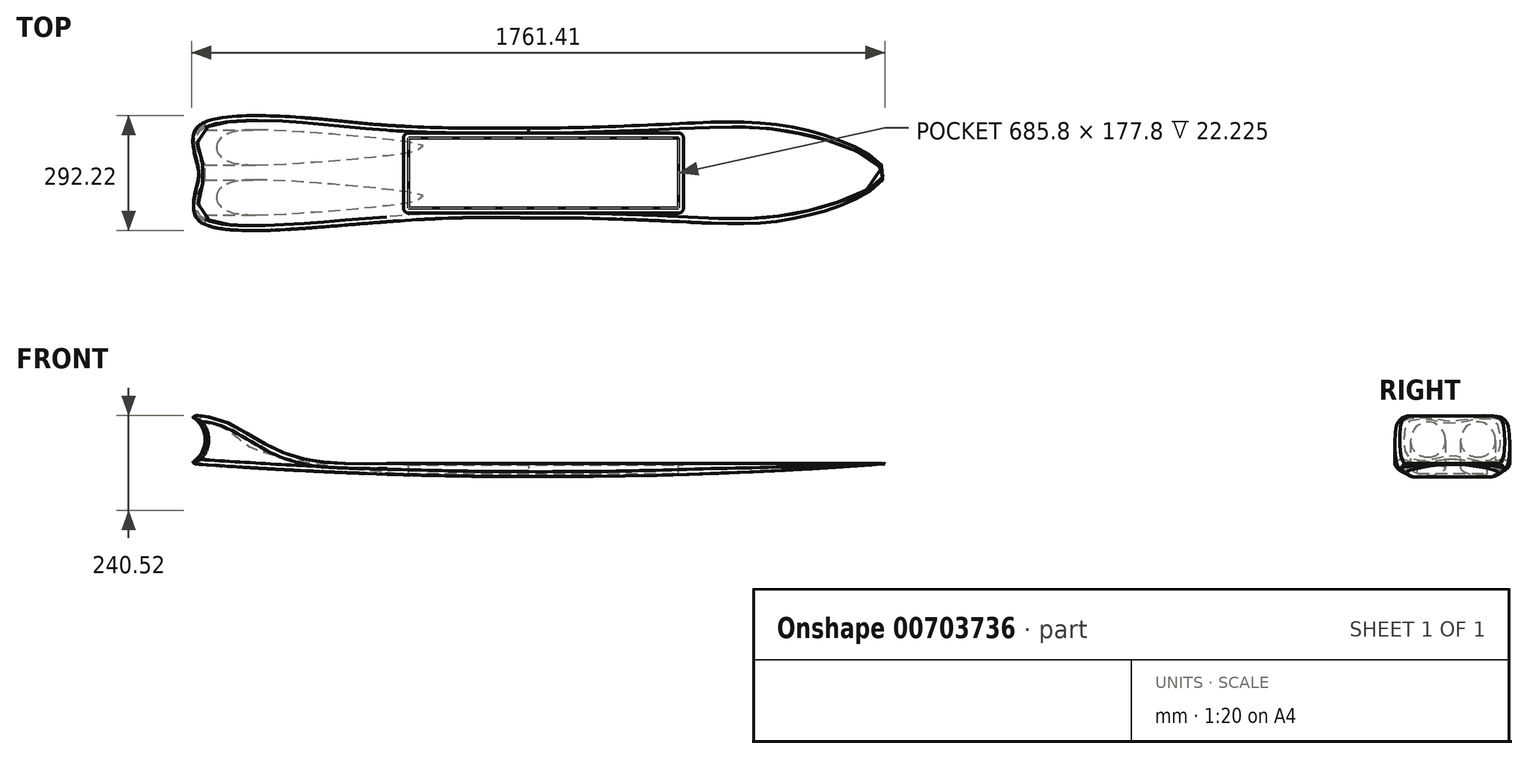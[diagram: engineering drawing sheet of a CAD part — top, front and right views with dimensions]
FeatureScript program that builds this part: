
annotation { "Feature Type Name" : "Feature", "Feature Type Description" : "" }
export const myFeature = defineFeature(function(context is Context, id is Id, definition is map)
    precondition{}
    {
        {
            var Q0;
            Q0=qCreatedBy(makeId("Front.planeOp"),FACE);
            var sketch = newSketch(context, id + "F0", { "sketchPlane" : qUnion([Q0])});
            skArc(sketch, "E0", {"start": v(-860.12, 0) * mm, "mid": v(28.88, -33.4) * mm, "end": v(917.88, 0) * mm});
            skArc(sketch, "E1", {"start": v(-860.12, 0) * mm, "mid": v(-821.37, 62.98) * mm, "end": v(-864.4, 123.1) * mm});
            skLineSegment(sketch, "E2", {"start": v(-360.96, 0) * mm, "end": v(917.88, 0) * mm});
            skFitSpline(sketch, "E3", {"points": [v(-864.4, 123.1) * mm, v(-768.9, 105.74) * mm, v(-612.6, 23.25) * mm, v(-360.96, 0) * mm], "startDerivative": vector(368.4, -19.72) * mm, "endDerivative": vector(657.62, 11.35) * mm});
            skSolve(sketch);
        }
        {
            var Q0;
            Q0=makeQuery(id+"F0.imprint","IMPRINT",FACE,{"disambiguationData":[TD([[makeQuery(id+"F0.imprint","IMPRINT",EDGE,{"derivedFrom":sQuery(id+"F0.wireOp",EDGE,"E0")}),1.0]])]});
            extrude(context, id + "F1", {"entities" : qUnion([Q0]), "endBound" : BoundingType.SYMMETRIC, "depth" : 304.8 * mm, "offsetDistance" : 25.4 * mm});
        }
        {
            var Q0;
            Q0=qCreatedBy(makeId("Top.planeOp"),FACE);
            var sketch = newSketch(context, id + "F2", { "sketchPlane" : qUnion([Q0])});
            skFitSpline(sketch, "E4", {"points": [v(0, 114.3) * mm, v(-558.8, 139.7) * mm, v(-838.2, 120.65) * mm, v(-852.96, 59.7) * mm, v(-838.2, 0) * mm, v(-850.9, -59.7) * mm, v(-838.2, -120.65) * mm, v(-558.8, -139.7) * mm, v(0, -114.3) * mm], "startDerivative": vector(-4957.76, -51.43) * mm, "endDerivative": vector(3133.64, -106.94) * mm});
            skFitSpline(sketch, "E5", {"points": [v(0, 114.3) * mm, v(685.8, 114.3) * mm, v(914.4, 0) * mm, v(685.8, -114.3) * mm, v(0, -114.3) * mm], "startDerivative": vector(3821.37, 9.43) * mm, "endDerivative": vector(-3821.37, -30.54) * mm});
            skLineSegment(sketch, "E6.bottom", {"start": v(-1371.02, 605.3) * mm, "end": v(1425.25, 605.3) * mm});
            skLineSegment(sketch, "E6.top", {"start": v(-1371.02, -634.77) * mm, "end": v(1425.25, -634.77) * mm});
            skLineSegment(sketch, "E6.left", {"start": v(-1371.02, 605.3) * mm, "end": v(-1371.02, -634.77) * mm});
            skLineSegment(sketch, "E6.right", {"start": v(1425.25, 605.3) * mm, "end": v(1425.25, -634.77) * mm});
            skSolve(sketch);
        }
        {
            var Q0;
            Q0=makeQuery(id+"F2.imprint","IMPRINT",FACE,{"disambiguationData":[TD([[makeQuery(id+"F2.imprint","IMPRINT",EDGE,{"derivedFrom":sQuery(id+"F2.wireOp",EDGE,"E4")}),-1.0]])]});
            extrude(context, id + "F3", {"entities" : qUnion([Q0]), "operationType" : NewBodyOperationType.REMOVE, "endBound" : BoundingType.SYMMETRIC, "depth" : 304.8 * mm, "offsetDistance" : 25.4 * mm});
        }
        {
            var Q0;
            Q0=makeQuery(id+"F3.boolean.opBoolean","INTERSECT",EDGE,{"derivedFrom":[makeQuery(id+"F1.opExtrude","SWEPT_FACE",FACE,{"disambiguationData":[OSD([sQuery(id+"F0.wireOp",EDGE,"E0")])]}),makeQuery(id+"F3.opExtrude","SWEPT_FACE",FACE,{"disambiguationData":[OSD([sQuery(id+"F2.wireOp",EDGE,"E4")])]})]});
            var Q1;
            Q1=makeQuery(id+"F3.boolean.opBoolean","INTERSECT",EDGE,{"derivedFrom":[makeQuery(id+"F1.opExtrude","SWEPT_FACE",FACE,{"disambiguationData":[OSD([sQuery(id+"F0.wireOp",EDGE,"E3")])]}),makeQuery(id+"F3.opExtrude","SWEPT_FACE",FACE,{"disambiguationData":[OSD([sQuery(id+"F2.wireOp",EDGE,"E4")])]})]});
            var Q2;
            Q2=makeQuery(id+"F1.opExtrude","SWEPT_FACE",FACE,{"disambiguationData":[OSD([sQuery(id+"F0.wireOp",EDGE,"E0")])]});
            var Q3;
            Q3=makeQuery(id+"F3.boolean.opBoolean","COPY",FACE,{"derivedFrom":makeQuery(id+"F3.opExtrude","SWEPT_FACE",FACE,{"disambiguationData":[OSD([sQuery(id+"F2.wireOp",EDGE,"E5")])]})});
            var Q4;
            Q4=makeQuery(id+"F3.boolean.opBoolean","COPY",FACE,{"derivedFrom":makeQuery(id+"F3.opExtrude","SWEPT_FACE",FACE,{"disambiguationData":[OSD([sQuery(id+"F2.wireOp",EDGE,"E4")])]})});
            var Q5;
            Q5=makeQuery(id+"F1.opExtrude","SWEPT_FACE",FACE,{"disambiguationData":[OSD([sQuery(id+"F0.wireOp",EDGE,"E2")])]});
            var Q6;
            Q6=makeQuery(id+"F3.boolean.opBoolean","INTERSECT",EDGE,{"derivedFrom":[makeQuery(id+"F1.opExtrude","SWEPT_FACE",FACE,{"disambiguationData":[OSD([sQuery(id+"F0.wireOp",EDGE,"E2")])]}),makeQuery(id+"F3.opExtrude","SWEPT_FACE",FACE,{"disambiguationData":[OSD([sQuery(id+"F2.wireOp",EDGE,"E5")])]})]});
            var Q7;
            Q7=makeQuery(id+"F3.boolean.opBoolean","INTERSECT",EDGE,{"derivedFrom":[makeQuery(id+"F1.opExtrude","SWEPT_FACE",FACE,{"disambiguationData":[OSD([sQuery(id+"F0.wireOp",EDGE,"E0")])]}),makeQuery(id+"F3.opExtrude","SWEPT_FACE",FACE,{"disambiguationData":[OSD([sQuery(id+"F2.wireOp",EDGE,"E5")])]})]});
            var Q8;
            Q8=makeQuery(id+"F1.opExtrude","SWEPT_FACE",FACE,{"disambiguationData":[OSD([sQuery(id+"F0.wireOp",EDGE,"E3")])]});
            var Q9;
            Q9=makeQuery(id+"F1.opExtrude","SWEPT_FACE",FACE,{"disambiguationData":[OSD([sQuery(id+"F0.wireOp",EDGE,"E1")])]});
            var Q10;
            Q10=makeQuery(id+"F3.boolean.opBoolean","INTERSECT",EDGE,{"derivedFrom":[makeQuery(id+"F1.opExtrude","SWEPT_FACE",FACE,{"disambiguationData":[OSD([sQuery(id+"F0.wireOp",EDGE,"E1")])]}),makeQuery(id+"F3.opExtrude","SWEPT_FACE",FACE,{"disambiguationData":[OSD([sQuery(id+"F2.wireOp",EDGE,"E4")])]})]});
            var Q11;
            Q11=makeQuery(id+"F1.opExtrude","SWEPT_EDGE",EDGE,{"disambiguationData":[OSD([sQuery(id+"F0.wireOp",EDGE,"E2"),sQuery(id+"F0.wireOp",EDGE,"E3")])]});
            var Q12;
            Q12=makeQuery(id+"F3.boolean.opBoolean","INTERSECT",EDGE,{"disambiguationData":[OD(0.0)],"derivedFrom":[makeQuery(id+"F1.opExtrude","SWEPT_FACE",FACE,{"disambiguationData":[OSD([sQuery(id+"F0.wireOp",EDGE,"E2")])]}),makeQuery(id+"F3.opExtrude","SWEPT_FACE",FACE,{"disambiguationData":[OSD([sQuery(id+"F2.wireOp",EDGE,"E4")])]})]});
            var Q13;
            {var subQ0=sQuery(id+"F2.wireOp",EDGE,"E5");var subQ1=sQuery(id+"F2.wireOp",EDGE,"E4");Q13=makeQuery(id+"F3.boolean.opBoolean","COPY",EDGE,{"derivedFrom":makeQuery(id+"F3.opExtrude","SWEPT_EDGE",EDGE,{"disambiguationData":[OSD([subQ1,subQ0]),TDD([makeQuery(id+"F2.imprint","INTERSECT",VERTEX,{"disambiguationData":[OD(0.0)],"derivedFrom":[subQ1,subQ0]})])]})});}
            var Q14;
            {var subQ0=sQuery(id+"F2.wireOp",EDGE,"E5");var subQ1=sQuery(id+"F2.wireOp",EDGE,"E4");Q14=makeQuery(id+"F3.boolean.opBoolean","COPY",EDGE,{"derivedFrom":makeQuery(id+"F3.opExtrude","SWEPT_EDGE",EDGE,{"disambiguationData":[OSD([subQ1,subQ0]),TDD([makeQuery(id+"F2.imprint","INTERSECT",VERTEX,{"disambiguationData":[OD(1.0)],"derivedFrom":[subQ1,subQ0]})])]})});}
            var Q15;
            Q15=makeQuery(id+"F3.boolean.opBoolean","INTERSECT",EDGE,{"disambiguationData":[OD(1.0)],"derivedFrom":[makeQuery(id+"F1.opExtrude","SWEPT_FACE",FACE,{"disambiguationData":[OSD([sQuery(id+"F0.wireOp",EDGE,"E2")])]}),makeQuery(id+"F3.opExtrude","SWEPT_FACE",FACE,{"disambiguationData":[OSD([sQuery(id+"F2.wireOp",EDGE,"E4")])]})]});
            fillet(context, id + "F4", {"entities" : qUnion([Q0, Q1, Q2, Q3, Q4, Q5, Q6, Q7, Q8, Q9, Q10, Q11, Q12, Q13, Q14, Q15]), "radius" : 12.7 * mm, "tangentPropagation" : true, "allowEdgeOverflow" : false});
        }
        {
            var Q0;
            Q0=makeQuery(id+"F1.opExtrude","SWEPT_FACE",FACE,{"disambiguationData":[OSD([sQuery(id+"F0.wireOp",EDGE,"E2")])]});
            var sketch = newSketch(context, id + "F5", { "sketchPlane" : qUnion([Q0])});
            skLineSegment(sketch, "E7.bottom", {"start": v(-304.8, -88.9) * mm, "end": v(381, -88.9) * mm});
            skLineSegment(sketch, "E7.top", {"start": v(-304.8, 88.9) * mm, "end": v(381, 88.9) * mm});
            skLineSegment(sketch, "E7.left", {"start": v(-304.8, -88.9) * mm, "end": v(-304.8, 88.9) * mm});
            skLineSegment(sketch, "E7.right", {"start": v(381, -88.9) * mm, "end": v(381, 88.9) * mm});
            skSolve(sketch);
        }
        {
            var Q0;
            Q0=makeQuery(id+"F5.imprint","IMPRINT",FACE,{"disambiguationData":[TD([[makeQuery(id+"F5.imprint","IMPRINT",EDGE,{"derivedFrom":sQuery(id+"F5.wireOp",EDGE,"E7.bottom")}),1.0]])]});
            extrude(context, id + "F6", {"entities" : qUnion([Q0]), "operationType" : NewBodyOperationType.REMOVE, "oppositeDirection" : true, "depth" : 25.4 * mm, "offsetDistance" : 25.4 * mm});
        }
        {
            var Q0;
            Q0=makeQuery(id+"F1.opExtrude","SWEPT_FACE",FACE,{"disambiguationData":[OSD([sQuery(id+"F0.wireOp",EDGE,"E2")])]});
            var sketch = newSketch(context, id + "F7", { "sketchPlane" : qUnion([Q0])});
            skLineSegment(sketch, "E8.bottom", {"start": v(-304.8, -101.6) * mm, "end": v(381, -101.6) * mm});
            skLineSegment(sketch, "E8.top", {"start": v(-304.8, 101.6) * mm, "end": v(381, 101.6) * mm});
            skLineSegment(sketch, "E8.left", {"start": v(-317.5, -88.9) * mm, "end": v(-317.5, 88.9) * mm});
            skLineSegment(sketch, "E8.right", {"start": v(393.7, -88.9) * mm, "end": v(393.7, 88.9) * mm});
            skPoint(sketch, "E9.visualSharp", {"position": v(-317.5, 101.6) * mm});
            skArc(sketch, "E9.filletArc", {"start": v(-304.8, 101.6) * mm, "mid": v(-313.78, 97.88) * mm, "end": v(-317.5, 88.9) * mm});
            skPoint(sketch, "E10.visualSharp", {"position": v(-317.5, -101.6) * mm});
            skArc(sketch, "E10.filletArc", {"start": v(-317.5, -88.9) * mm, "mid": v(-313.78, -97.88) * mm, "end": v(-304.8, -101.6) * mm});
            skPoint(sketch, "E11.visualSharp", {"position": v(393.7, -101.6) * mm});
            skArc(sketch, "E11.filletArc", {"start": v(381, -101.6) * mm, "mid": v(389.98, -97.88) * mm, "end": v(393.7, -88.9) * mm});
            skPoint(sketch, "E12.visualSharp", {"position": v(393.7, 101.6) * mm});
            skArc(sketch, "E12.filletArc", {"start": v(393.7, 88.9) * mm, "mid": v(389.98, 97.88) * mm, "end": v(381, 101.6) * mm});
            skSolve(sketch);
        }
        {
            var Q0;
            Q0 = qSketchRegion(id + "F7", true);
            extrude(context, id + "F8", {"entities" : qUnion([Q0]), "operationType" : NewBodyOperationType.REMOVE, "oppositeDirection" : true, "depth" : 3.17 * mm, "offsetDistance" : 25.4 * mm});
        }
        {
            var Q0;
            {var subQ0=makeQuery(id+"F3.opExtrude","SWEPT_FACE",FACE,{"disambiguationData":[OSD([sQuery(id+"F2.wireOp",EDGE,"E4")])]});Q0=makeQuery(id+"F4.opFillet","BLEND_VERTEX",VERTEX,{"disambiguationData":[OD(0.0)],"blendedFrom":[makeQuery(id+"F3.boolean.opBoolean","INTERSECT",EDGE,{"derivedFrom":[makeQuery(id+"F1.opExtrude","SWEPT_FACE",FACE,{"disambiguationData":[OSD([sQuery(id+"F0.wireOp",EDGE,"E1")])]}),subQ0]}),makeQuery(id+"F3.boolean.opBoolean","INTERSECT",EDGE,{"derivedFrom":[makeQuery(id+"F1.opExtrude","SWEPT_FACE",FACE,{"disambiguationData":[OSD([sQuery(id+"F0.wireOp",EDGE,"E3")])]}),subQ0]}),makeQuery(id+"F3.boolean.opBoolean","COPY",FACE,{"derivedFrom":subQ0})],"blendedInto":[makeQuery(id+"F3.boolean.opBoolean","COPY",FACE,{"derivedFrom":subQ0})]});}
            var Q1;
            {var subQ0=makeQuery(id+"F3.opExtrude","SWEPT_FACE",FACE,{"disambiguationData":[OSD([sQuery(id+"F2.wireOp",EDGE,"E4")])]});Q1=makeQuery(id+"F4.opFillet","BLEND_VERTEX",VERTEX,{"disambiguationData":[OD(0.0)],"blendedFrom":[makeQuery(id+"F3.boolean.opBoolean","INTERSECT",EDGE,{"derivedFrom":[makeQuery(id+"F1.opExtrude","SWEPT_FACE",FACE,{"disambiguationData":[OSD([sQuery(id+"F0.wireOp",EDGE,"E1")])]}),subQ0]}),makeQuery(id+"F3.boolean.opBoolean","INTERSECT",EDGE,{"derivedFrom":[makeQuery(id+"F1.opExtrude","SWEPT_FACE",FACE,{"disambiguationData":[OSD([sQuery(id+"F0.wireOp",EDGE,"E0")])]}),subQ0]}),makeQuery(id+"F3.boolean.opBoolean","COPY",FACE,{"derivedFrom":subQ0})],"blendedInto":[makeQuery(id+"F3.boolean.opBoolean","COPY",FACE,{"derivedFrom":subQ0})]});}
            var Q2;
            {var subQ0=makeQuery(id+"F3.opExtrude","SWEPT_FACE",FACE,{"disambiguationData":[OSD([sQuery(id+"F2.wireOp",EDGE,"E4")])]});Q2=makeQuery(id+"F4.opFillet","BLEND_VERTEX",VERTEX,{"disambiguationData":[OD(1.0)],"blendedFrom":[makeQuery(id+"F3.boolean.opBoolean","INTERSECT",EDGE,{"derivedFrom":[makeQuery(id+"F1.opExtrude","SWEPT_FACE",FACE,{"disambiguationData":[OSD([sQuery(id+"F0.wireOp",EDGE,"E1")])]}),subQ0]}),makeQuery(id+"F3.boolean.opBoolean","INTERSECT",EDGE,{"derivedFrom":[makeQuery(id+"F1.opExtrude","SWEPT_FACE",FACE,{"disambiguationData":[OSD([sQuery(id+"F0.wireOp",EDGE,"E3")])]}),subQ0]}),makeQuery(id+"F3.boolean.opBoolean","COPY",FACE,{"derivedFrom":subQ0})],"blendedInto":[makeQuery(id+"F3.boolean.opBoolean","COPY",FACE,{"derivedFrom":subQ0})]});}
            cPlane(context, id + "F9", {"entities" : qUnion([Q0, Q1, Q2]), "cplaneType" : CPlaneType.THREE_POINT, "offset" : 25.4 * mm, "width" : 152.4 * mm, "height" : 152.4 * mm});
        }
        {
            var Q0;
            Q0=qCreatedBy(id+"F9.planeOp",FACE);
            var sketch = newSketch(context, id + "F10", { "sketchPlane" : qUnion([Q0])});
            skCircle(sketch, "E13", {"center": v(63.5, 28.58) * mm, "radius": 44.45 * mm});
            skCircle(sketch, "E14.MirrorC", {"center": v(-63.5, 28.58) * mm, "radius": 44.45 * mm});
            skSolve(sketch);
        }
        {
            var Q0;
            Q0=qCreatedBy(makeId("Front.planeOp"),FACE);
            var sketch = newSketch(context, id + "F11", { "sketchPlane" : qUnion([Q0])});
            skFitSpline(sketch, "E15", {"points": [v(-914.37, 65.91) * mm, v(-795.96, 53.69) * mm, v(-716.48, 0) * mm, v(-155.83, -76.63) * mm], "startDerivative": vector(444.02, -13.56) * mm, "endDerivative": vector(817.54, -12.02) * mm});
            skSolve(sketch);
        }
        {
            var Q0;
            Q0 = qSketchRegion(id + "F10", true);
            var Q1;
            Q1 = qConstructionFilter(qBodyType(qCreatedBy(id + "F11" ,EDGE), BodyType.WIRE), ConstructionObject.NO);
            sweep(context, id + "F12", {"operationType" : NewBodyOperationType.REMOVE, "profiles" : qUnion([Q0]), "path" : qUnion([Q1])});
        }
    });
